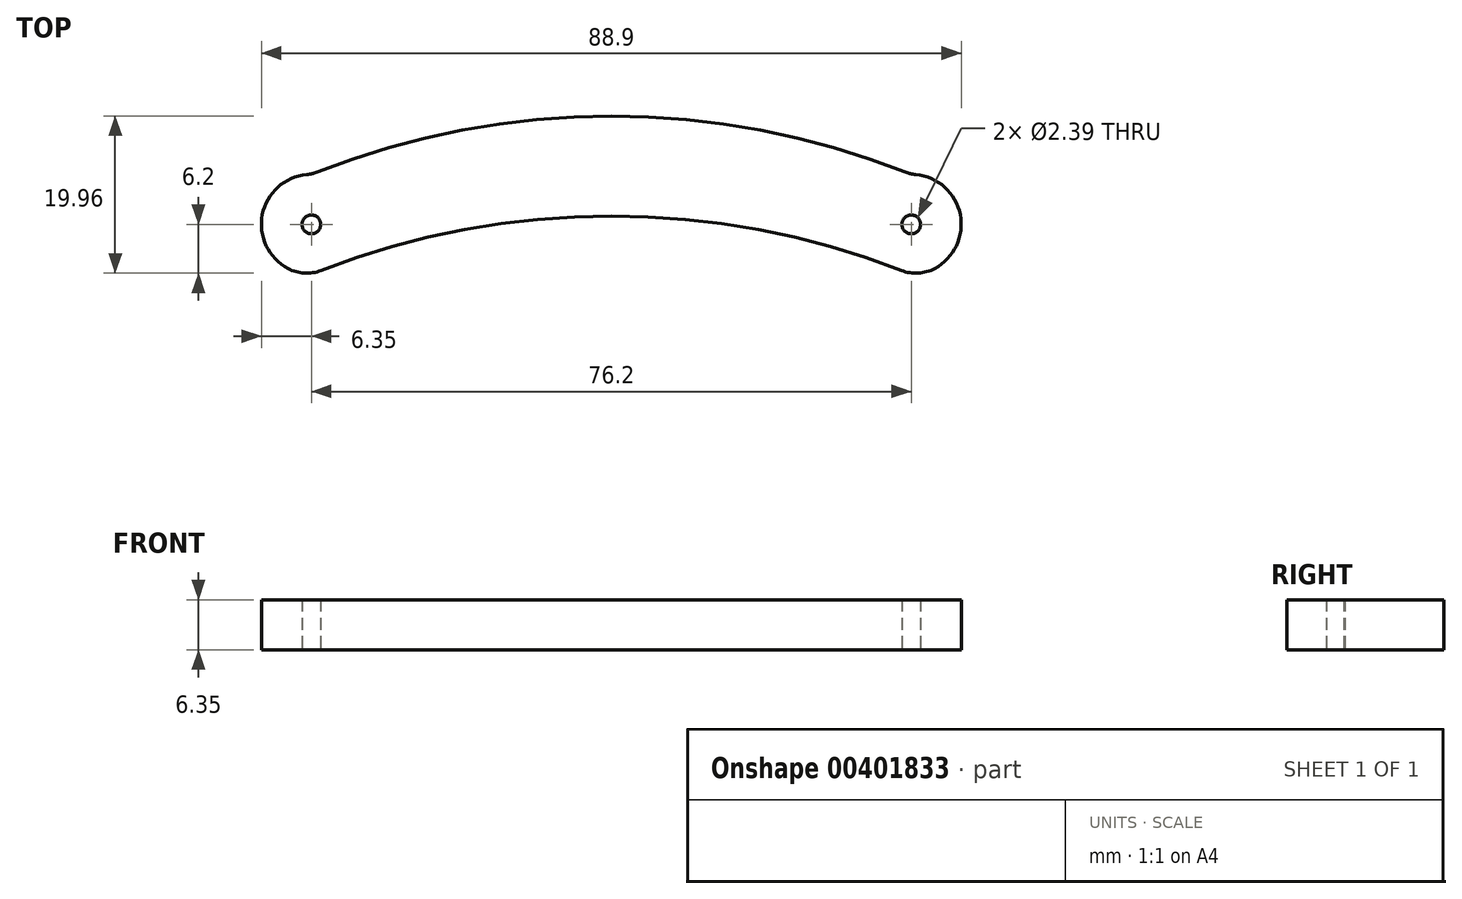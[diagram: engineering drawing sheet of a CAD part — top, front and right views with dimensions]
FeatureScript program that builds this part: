
annotation { "Feature Type Name" : "Feature", "Feature Type Description" : "" }
export const myFeature = defineFeature(function(context is Context, id is Id, definition is map)
    precondition{}
    {
        {
            var Q0;
            Q0=qCreatedBy(makeId("Top.planeOp"),FACE);
            var sketch = newSketch(context, id + "F0", { "sketchPlane" : qUnion([Q0])});
            skLineSegment(sketch, "E0.bottom", {"start": v(-38.1, 6.35) * mm, "end": v(38.1, 6.35) * mm, "construction": true});
            skLineSegment(sketch, "E0.top", {"start": v(-38.1, -6.35) * mm, "end": v(38.1, -6.35) * mm, "construction": true});
            skLineSegment(sketch, "E0.left", {"start": v(-38.1, 6.35) * mm, "end": v(-38.1, -6.35) * mm, "construction": true});
            skLineSegment(sketch, "E0.right", {"start": v(38.1, 6.35) * mm, "end": v(38.1, -6.35) * mm, "construction": true});
            skPoint(sketch, "E0.middle", {"position": v(0, 0) * mm});
            skCircle(sketch, "E1", {"center": v(-38.1, 0) * mm, "radius": 1.2 * mm});
            skCircle(sketch, "E2", {"center": v(38.1, 0) * mm, "radius": 1.2 * mm});
            skArc(sketch, "E3", {"start": v(-38.1, 6.35) * mm, "mid": v(-44.45, 0) * mm, "end": v(-38.1, -6.35) * mm});
            skArc(sketch, "E4", {"start": v(38.1, 6.35) * mm, "mid": v(44.45, 0) * mm, "end": v(38.1, -6.35) * mm});
            skArc(sketch, "E5", {"start": v(38.1, 6.35) * mm, "mid": v(0, 13.76) * mm, "end": v(-38.1, 6.35) * mm});
            skArc(sketch, "E6", {"start": v(38.1, -6.35) * mm, "mid": v(0, 1.06) * mm, "end": v(-38.1, -6.35) * mm});
            skSolve(sketch);
        }
        {
            var Q0;
            Q0 = qSketchRegion(id + "F0", true);
            extrude(context, id + "F1", {"entities" : qUnion([Q0]), "depth" : 6.35 * mm});
        }
        {
            var Q0;
            Q0=makeQuery(id+"F1.opExtrude","SWEPT_EDGE",EDGE,{"disambiguationData":[OSD([sQuery(id+"F0.wireOp",EDGE,"E3"),sQuery(id+"F0.wireOp",EDGE,"E6")])]});
            var Q1;
            Q1=makeQuery(id+"F1.opExtrude","SWEPT_EDGE",EDGE,{"disambiguationData":[OSD([sQuery(id+"F0.wireOp",EDGE,"E4"),sQuery(id+"F0.wireOp",EDGE,"E6")])]});
            var Q2;
            Q2=makeQuery(id+"F1.opExtrude","SWEPT_EDGE",EDGE,{"disambiguationData":[OSD([sQuery(id+"F0.wireOp",EDGE,"E4"),sQuery(id+"F0.wireOp",EDGE,"E5")])]});
            var Q3;
            Q3=makeQuery(id+"F1.opExtrude","SWEPT_EDGE",EDGE,{"disambiguationData":[OSD([sQuery(id+"F0.wireOp",EDGE,"E3"),sQuery(id+"F0.wireOp",EDGE,"E5")])]});
            fillet(context, id + "F2", {"entities" : qUnion([Q0, Q1, Q2, Q3]), "radius" : 5.08 * mm, "tangentPropagation" : true, "allowEdgeOverflow" : false});
        }
    });
